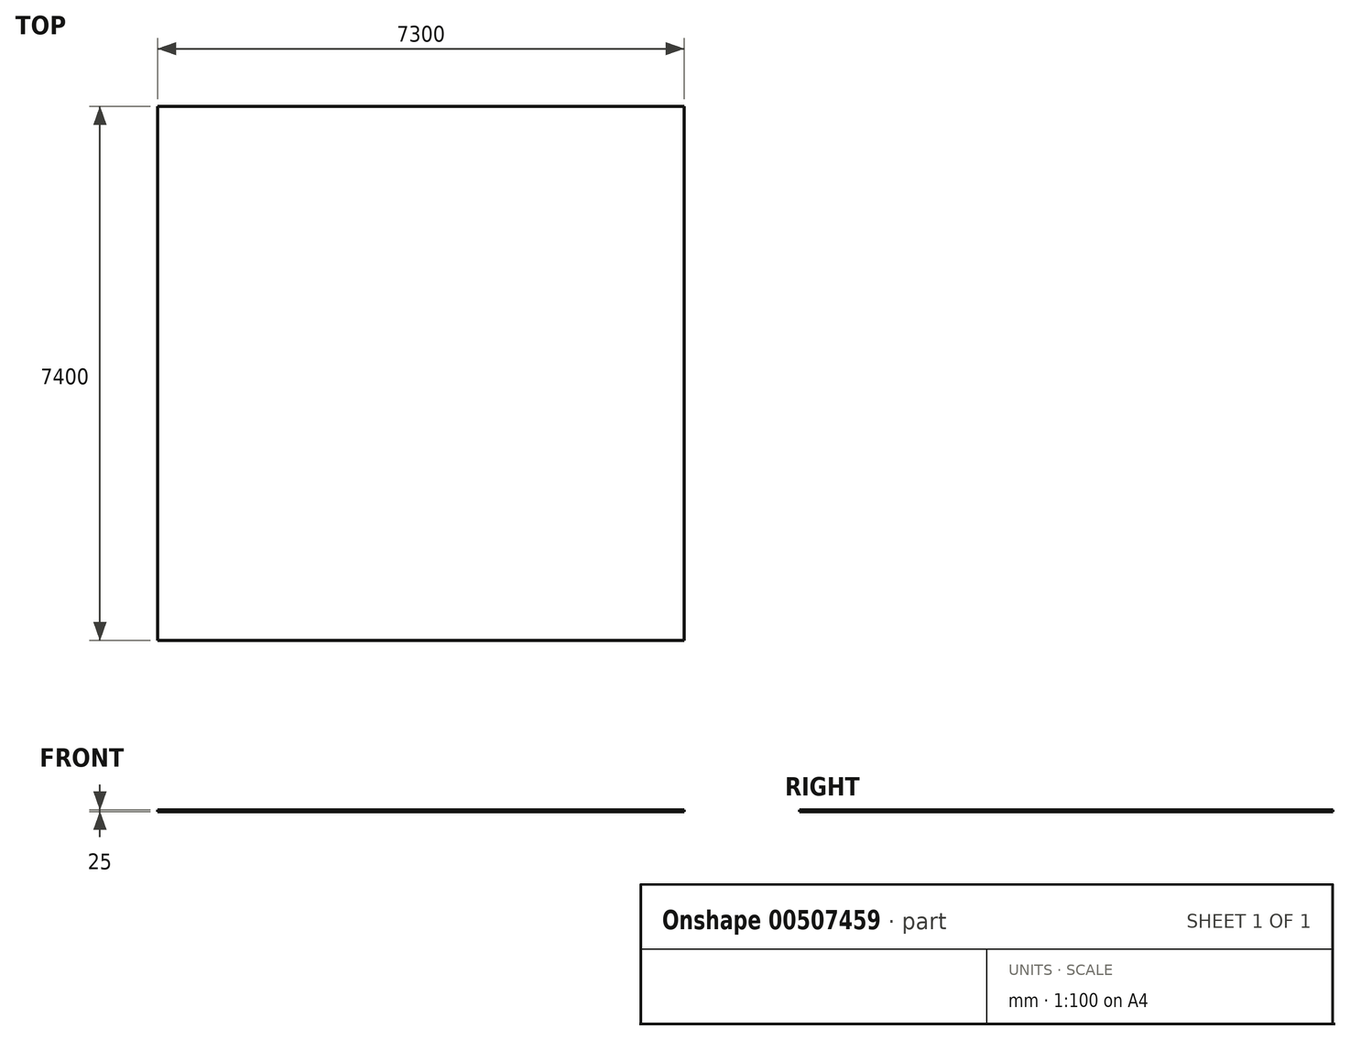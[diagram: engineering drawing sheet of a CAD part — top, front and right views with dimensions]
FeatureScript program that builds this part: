
annotation { "Feature Type Name" : "Feature", "Feature Type Description" : "" }
export const myFeature = defineFeature(function(context is Context, id is Id, definition is map)
    precondition{}
    {
        {
            var Q0;
            Q0=qCreatedBy(makeId("Top.planeOp"),FACE);
            var sketch = newSketch(context, id + "F0", { "sketchPlane" : qUnion([Q0])});
            skLineSegment(sketch, "E0.bottom", {"start": v(-3651.2, 5608.55) * mm, "end": v(3648.8, 5608.55) * mm});
            skLineSegment(sketch, "E0.top", {"start": v(-3651.2, -1791.45) * mm, "end": v(3648.8, -1791.45) * mm});
            skLineSegment(sketch, "E0.left", {"start": v(-3651.2, 5608.55) * mm, "end": v(-3651.2, -1791.45) * mm});
            skLineSegment(sketch, "E0.right", {"start": v(3648.8, 5608.55) * mm, "end": v(3648.8, -1791.45) * mm});
            skLineSegment(sketch, "E1.bottom", {"start": v(1935.93, 5608.55) * mm, "end": v(-1240.42, 5608.55) * mm});
            skLineSegment(sketch, "E1.top", {"start": v(1935.93, 4025.27) * mm, "end": v(-1240.42, 4025.27) * mm});
            skLineSegment(sketch, "E1.left", {"start": v(1935.93, 5608.55) * mm, "end": v(1935.93, 4025.27) * mm});
            skLineSegment(sketch, "E1.right", {"start": v(-1240.42, 5608.55) * mm, "end": v(-1240.42, 4025.27) * mm});
            skSolve(sketch);
        }
        {
            var Q0;
            Q0 = qSketchRegion(id + "F0", true);
            extrude(context, id + "F1", {"entities" : qUnion([Q0]), "oppositeDirection" : true, "depth" : 25 * mm});
        }
    });
